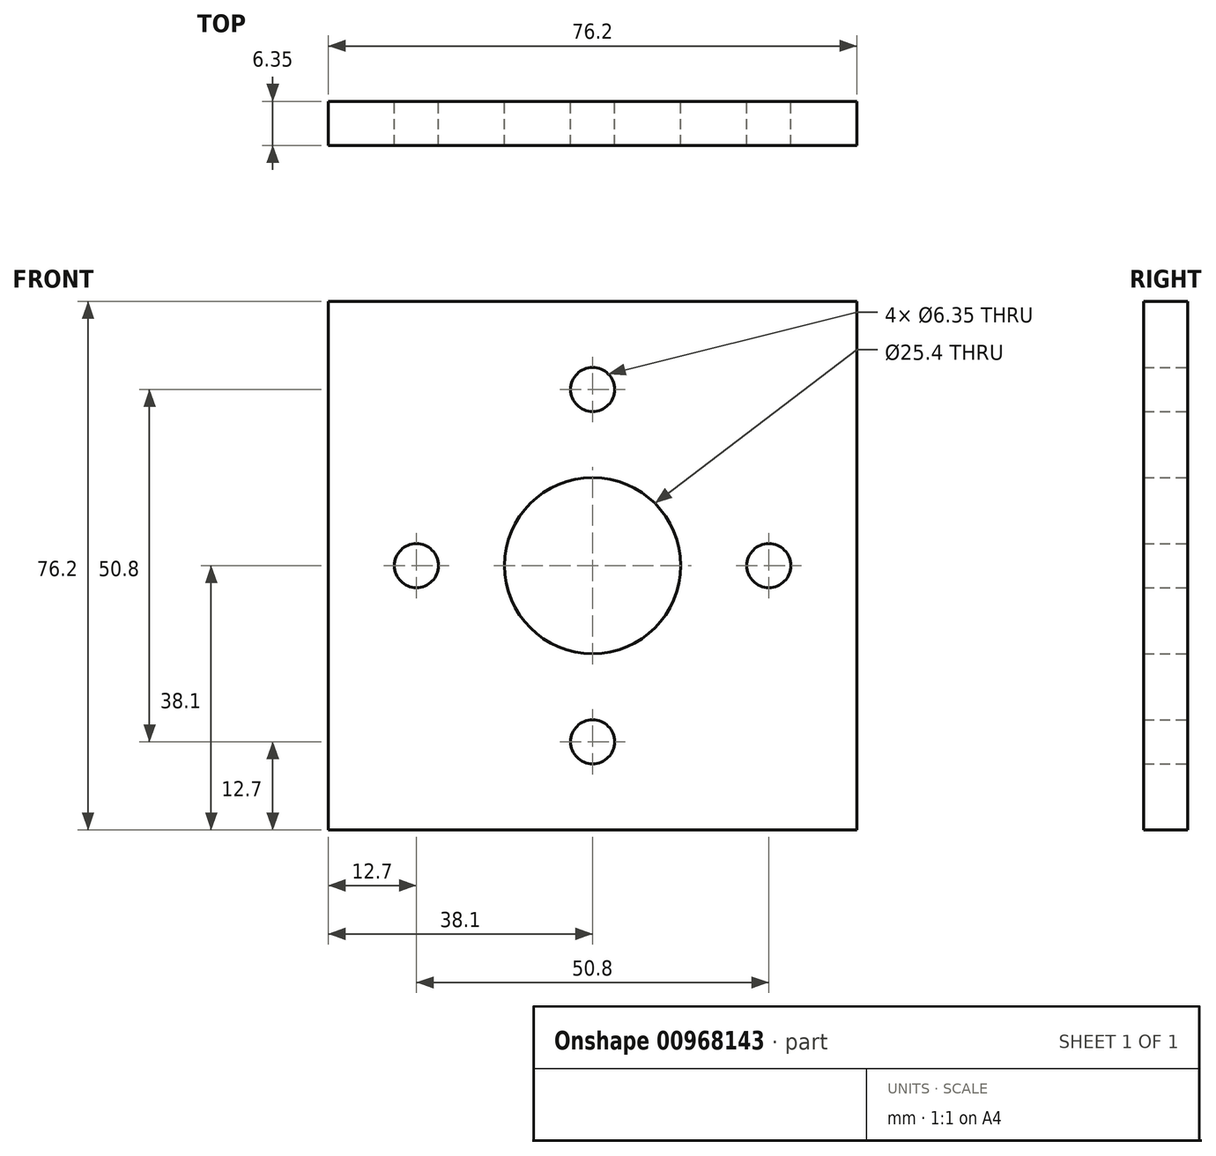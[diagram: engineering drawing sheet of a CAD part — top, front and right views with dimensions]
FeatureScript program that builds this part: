
annotation { "Feature Type Name" : "Feature", "Feature Type Description" : "" }
export const myFeature = defineFeature(function(context is Context, id is Id, definition is map)
    precondition{}
    {
        {
            var Q0;
            Q0=qCreatedBy(makeId("Front.planeOp"),FACE);
            var sketch = newSketch(context, id + "F0", { "sketchPlane" : qUnion([Q0])});
            skLineSegment(sketch, "E0.bottom", {"start": v(38.1, 38.1) * mm, "end": v(-38.1, 38.1) * mm});
            skLineSegment(sketch, "E0.top", {"start": v(38.1, -38.1) * mm, "end": v(-38.1, -38.1) * mm});
            skLineSegment(sketch, "E0.left", {"start": v(38.1, 38.1) * mm, "end": v(38.1, -38.1) * mm});
            skLineSegment(sketch, "E0.right", {"start": v(-38.1, 38.1) * mm, "end": v(-38.1, -38.1) * mm});
            skPoint(sketch, "E0.middle", {"position": v(0, 0) * mm});
            skCircle(sketch, "E1", {"center": v(0, 0) * mm, "radius": 12.7 * mm});
            skCircle(sketch, "E2", {"center": v(0, 25.4) * mm, "radius": 3.18 * mm});
            skCircle(sketch, "E3", {"center": v(25.4, 0) * mm, "radius": 3.18 * mm});
            skCircle(sketch, "E4", {"center": v(0, -25.4) * mm, "radius": 3.18 * mm});
            skCircle(sketch, "E5", {"center": v(-25.4, 0) * mm, "radius": 3.18 * mm});
            skSolve(sketch);
        }
        {
            var Q0;
            Q0 = qSketchRegion(id + "F0", true);
            extrude(context, id + "F1", {"entities" : qUnion([Q0]), "depth" : 6.35 * mm, "offsetDistance" : 25.4 * mm});
        }
    });
